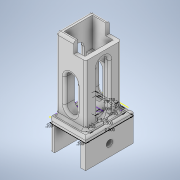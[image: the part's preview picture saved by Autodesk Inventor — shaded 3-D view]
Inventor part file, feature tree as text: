
AUTODESK INVENTOR PART (.ipt)
format: ipt  version: 2020 (Build 240168000, 168)  size: 309,248 bytes
history: native  units: in
note: dims shown in document units (in); Inventor stores cm internally (conversion verified against a paired STEP export)
features: extrude x7, sketch x6, hole x1, fillet x1
ambient origin geometry x8: Origin, YZ Plane, XZ Plane, XY Plane, X Axis, Y Axis, Z Axis, Center Point
bodies: Solid1 (feature_tree)
feature tree (15):
  sketch  "Sketch1"  dims[d0=1.5in d1=2.0in]
  extrude  "Extrusion1"  Depth=2.0in
  extrude  "Extrusion2"  Depth=0.2in
  hole  "Hole1"  [1 undecoded]
  sketch  "Sketch3"  dims[d4=1.0in d5=0.0in d6=0.2in d7=0.0in]
  extrude  "Extrusion3"  Depth=1.0in
  extrude  "Extrusion4"  Depth=0.1in
  extrude  "Extrusion5"  Depth=0.1in
  extrude  "Extrusion6"  Depth=0.1in
  extrude  "Extrusion7"  Depth=0.1in
  fillet  "Fillet1"  Radius=0.25in
  sketch  "Sketch2"  dims[d2=0.2in d3=0.2in]
  sketch  "Sketch4"  dims[d8=0.5in]
  sketch  "Sketch5"  dims[d9=0.266in d10=0.75in d11=0.438in d12=0.25in d13=0.5635in d14=1.0in d15=0.8108in d16=1.0in]
  sketch  "Sketch6"  dims[d17=1.25in d18=1.5in d19=0.875in d20=1.1875in d21=0.25in d22=0.25in d23=3.0in d24=0.0in d25=1.7855in d26=0.0in d27=0.5in d28=0.465in d29=0.0in d30=0.625in d31=0.5in d32=90.0deg d33=1.0in d34=0.5in d35=2.0in d36=0.0in d37=0.5in d38=1.75in d39=0.5in d40=2.0in d41=0.0in d42=0.1in]
note: 1 required parameter value undecoded (feature->parameter linkage not recoverable at this tier; creation-order binding heuristic only, values carry confidence <= 0.55)
